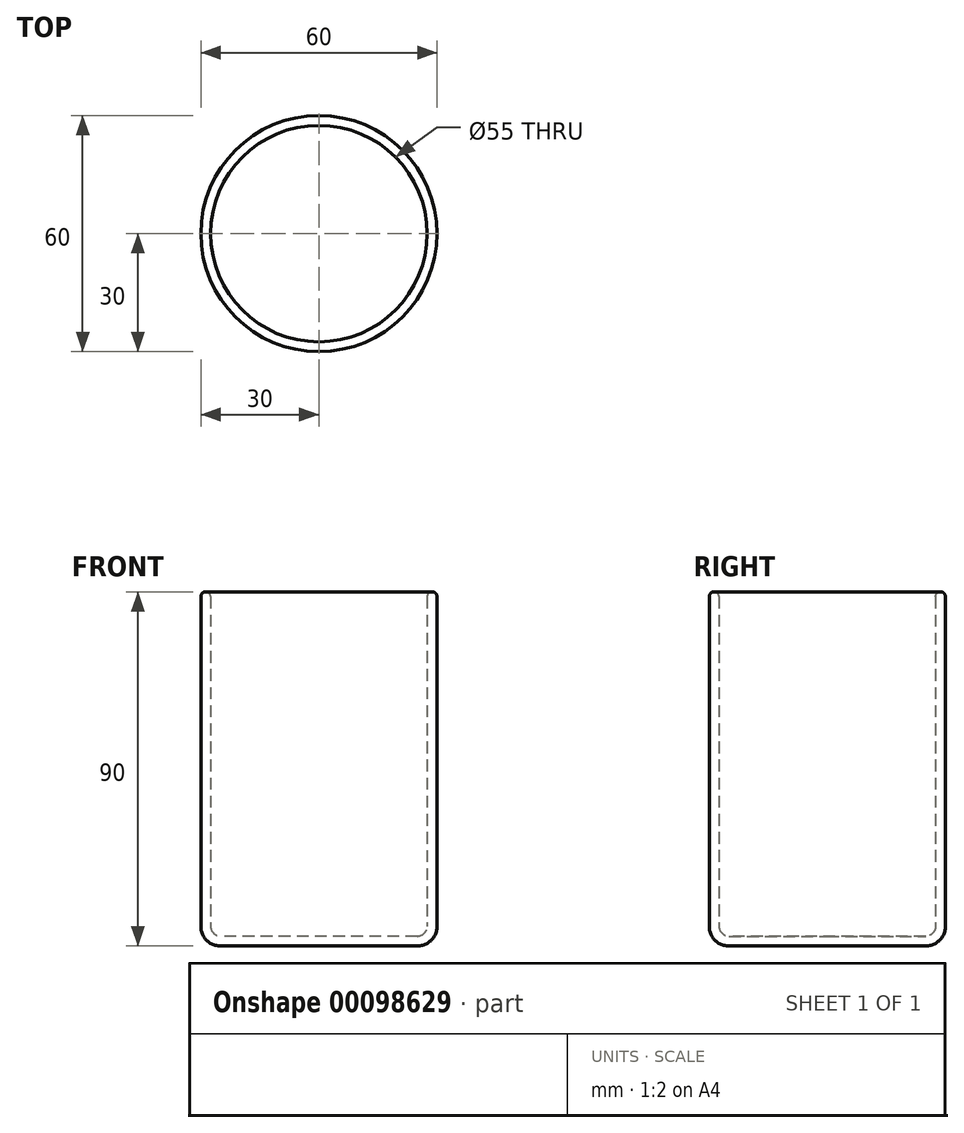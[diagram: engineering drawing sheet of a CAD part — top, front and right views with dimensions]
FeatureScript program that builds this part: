
annotation { "Feature Type Name" : "Feature", "Feature Type Description" : "" }
export const myFeature = defineFeature(function(context is Context, id is Id, definition is map)
    precondition{}
    {
        {
            var Q0;
            Q0=qCreatedBy(makeId("Top.planeOp"),FACE);
            var sketch = newSketch(context, id + "F0", { "sketchPlane" : qUnion([Q0])});
            skCircle(sketch, "E0", {"center": v(0, 0) * mm, "radius": 30 * mm});
            skSolve(sketch);
        }
        {
            var Q0;
            Q0=makeQuery(id+"F0.imprint","IMPRINT",FACE,{"disambiguationData":[TD([[makeQuery(id+"F0.imprint","IMPRINT",EDGE,{"derivedFrom":sQuery(id+"F0.wireOp",EDGE,"E0")}),1.0]])]});
            extrude(context, id + "F1", {"entities" : qUnion([Q0]), "depth" : 90 * mm});
        }
        {
            var Q0;
            Q0=makeQuery(id+"F1.opExtrude","CAP_FACE",FACE,{"disambiguationData":[OSD([sQuery(id+"F0.wireOp",EDGE,"E0")])],"isStart":false});
            shell(context, id + "F2", {"entities" : qUnion([Q0]), "thickness" : 2.5 * mm});
        }
        {
            var Q0;
            {var subQ0=sQuery(id+"F0.wireOp",EDGE,"E0");Q0=makeQuery(id+"F2.opShell","OFFSET_EDGE",EDGE,{"disambiguationData":[OSD([subQ0]),TDD([makeQuery(id+"F1.opExtrude","CAP_EDGE",EDGE,{"disambiguationData":[OSD([subQ0])],"isStart":true})])]});}
            fillet(context, id + "F3", {"entities" : qUnion([Q0]), "radius" : 2.5 * mm, "tangentPropagation" : true, "allowEdgeOverflow" : false});
        }
        {
            var Q0;
            Q0=makeQuery(id+"F1.opExtrude","CAP_EDGE",EDGE,{"disambiguationData":[OSD([sQuery(id+"F0.wireOp",EDGE,"E0")])],"isStart":true});
            fillet(context, id + "F4", {"entities" : qUnion([Q0]), "radius" : 5 * mm, "tangentPropagation" : true, "allowEdgeOverflow" : false});
        }
        {
            var Q0;
            Q0=makeQuery(id+"F1.opExtrude","CAP_EDGE",EDGE,{"disambiguationData":[OSD([sQuery(id+"F0.wireOp",EDGE,"E0")])],"isStart":false});
            var Q1;
            {var subQ0=sQuery(id+"F0.wireOp",EDGE,"E0");Q1=makeQuery(id+"F2.opShell","OFFSET_EDGE",EDGE,{"disambiguationData":[OSD([subQ0]),TDD([makeQuery(id+"F1.opExtrude","CAP_EDGE",EDGE,{"disambiguationData":[OSD([subQ0])],"isStart":false})])]});}
            fillet(context, id + "F5", {"entities" : qUnion([Q0, Q1]), "radius" : 1.25 * mm, "tangentPropagation" : true, "allowEdgeOverflow" : false});
        }
    });
